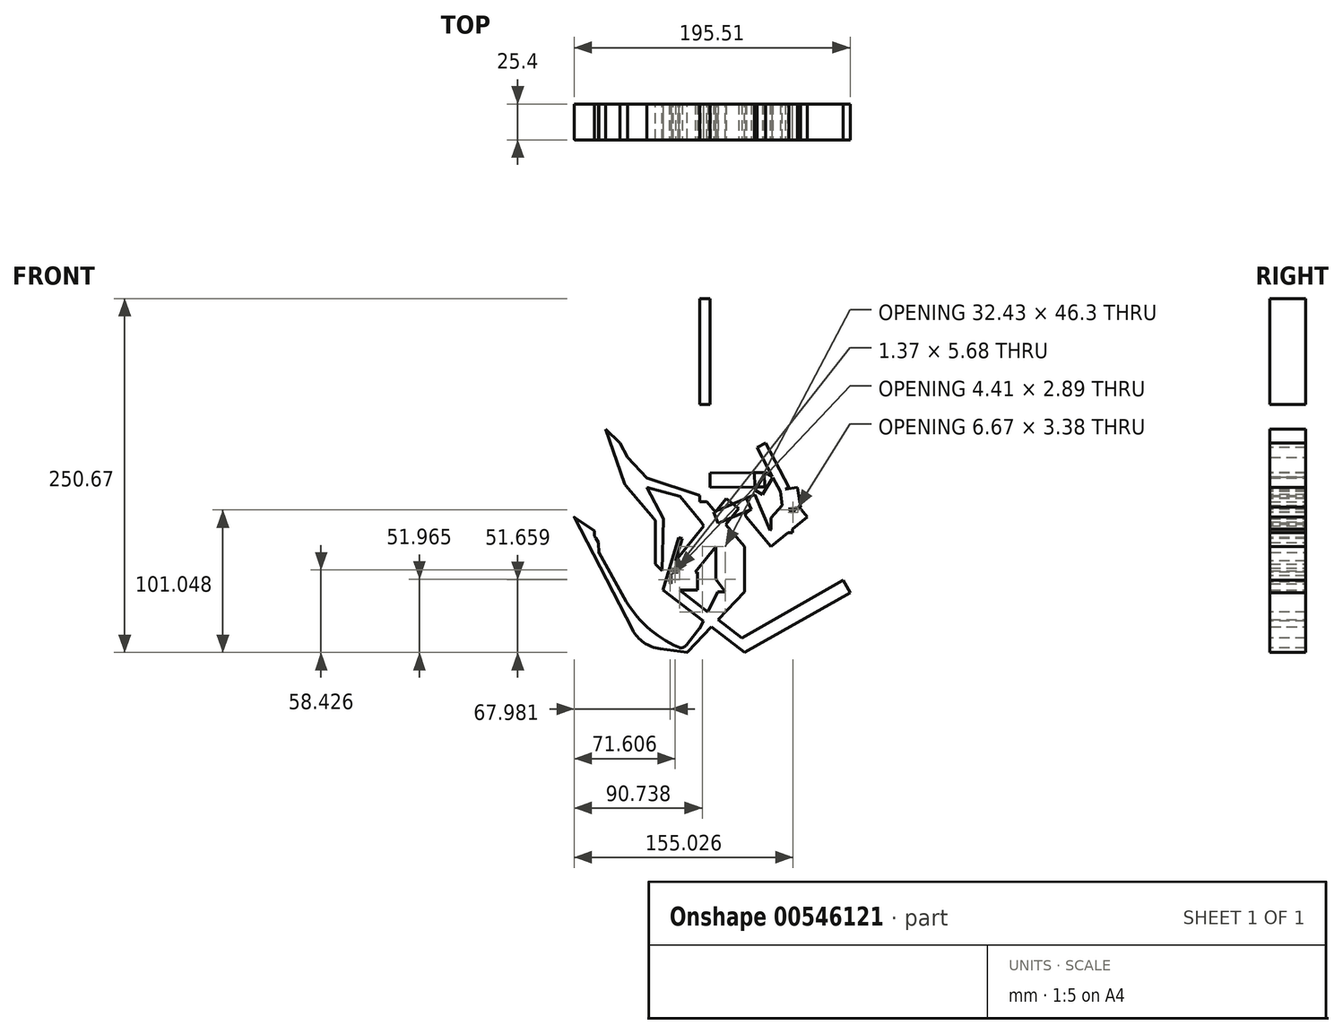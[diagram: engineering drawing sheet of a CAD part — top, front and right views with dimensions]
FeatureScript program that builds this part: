
annotation { "Feature Type Name" : "Feature", "Feature Type Description" : "" }
export const myFeature = defineFeature(function(context is Context, id is Id, definition is map)
    precondition{}
    {
        {
            var Q0;
            Q0=qCreatedBy(makeId("Front.planeOp"),FACE);
            var sketch = newSketch(context, id + "F0", { "sketchPlane" : qUnion([Q0])});
            skLineSegment(sketch, "E0", {"start": v(-82.74, 63.4) * mm, "end": v(-69.2, 48.58) * mm});
            skLineSegment(sketch, "E1", {"start": v(-69.2, 48.58) * mm, "end": v(-30.01, 35.76) * mm});
            skLineSegment(sketch, "E2", {"start": v(-30.01, 35.76) * mm, "end": v(0, 0) * mm});
            skLineSegment(sketch, "E3", {"start": v(0, 0) * mm, "end": v(0, -32.01) * mm});
            skLineSegment(sketch, "E4", {"start": v(0, -32.01) * mm, "end": v(-40.44, -74.7) * mm});
            skLineSegment(sketch, "E5", {"start": v(-40.44, -74.7) * mm, "end": v(-73.16, -70.67) * mm});
            skLineSegment(sketch, "E6", {"start": v(-73.16, -70.67) * mm, "end": v(-120.63, 20.91) * mm});
            skLineSegment(sketch, "E7", {"start": v(-120.63, 20.91) * mm, "end": v(-106.32, 11.13) * mm});
            skLineSegment(sketch, "E8", {"start": v(-106.32, 11.13) * mm, "end": v(-106.32, 7.38) * mm});
            skLineSegment(sketch, "E9", {"start": v(-106.32, 7.38) * mm, "end": v(-103.32, 2.97) * mm});
            skLineSegment(sketch, "E10", {"start": v(-103.32, 2.97) * mm, "end": v(-103.19, -3.97) * mm});
            skLineSegment(sketch, "E11", {"start": v(-103.19, -3.97) * mm, "end": v(-69.32, -65.1) * mm});
            skLineSegment(sketch, "E12", {"start": v(-69.32, -65.1) * mm, "end": v(-43.28, -72.68) * mm});
            skPoint(sketch, "E12.endSnap0", {"position": v(-56.8, -72.68) * mm});
            skLineSegment(sketch, "E13", {"start": v(-43.28, -72.68) * mm, "end": v(-31.05, -56.63) * mm});
            skLineSegment(sketch, "E14", {"start": v(-31.05, -56.63) * mm, "end": v(-19.08, -32.01) * mm});
            skLineSegment(sketch, "E15", {"start": v(-19.08, -32.01) * mm, "end": v(-19.08, -32.01) * mm});
            skLineSegment(sketch, "E16", {"start": v(-19.08, -32.01) * mm, "end": v(-13.68, -32.01) * mm});
            skLineSegment(sketch, "E17", {"start": v(-13.68, -32.01) * mm, "end": v(-20.13, -23.16) * mm});
            skLineSegment(sketch, "E18", {"start": v(-20.13, -23.16) * mm, "end": v(-20.13, 0) * mm});
            skLineSegment(sketch, "E19", {"start": v(-20.13, 0) * mm, "end": v(-30.68, 17.6) * mm});
            skLineSegment(sketch, "E20", {"start": v(-30.68, 17.6) * mm, "end": v(-45.8, 35.76) * mm});
            skLineSegment(sketch, "E21", {"start": v(-45.8, 35.76) * mm, "end": v(-69.2, 42.17) * mm});
            skPoint(sketch, "E21.endSnap0", {"position": v(-49.6, 42.17) * mm});
            skLineSegment(sketch, "E22", {"start": v(-69.2, 42.17) * mm, "end": v(-57.5, 19.66) * mm});
            skPoint(sketch, "E22.endSnap0", {"position": v(-57.5, 38.97) * mm});
            skLineSegment(sketch, "E23", {"start": v(-57.5, 19.66) * mm, "end": v(-58.4, -17.13) * mm});
            skLineSegment(sketch, "E24", {"start": v(-58.4, -17.13) * mm, "end": v(-63.03, -12.3) * mm});
            skLineSegment(sketch, "E25", {"start": v(-63.03, -12.3) * mm, "end": v(-63.03, 18.72) * mm});
            skLineSegment(sketch, "E26", {"start": v(-63.03, 18.72) * mm, "end": v(-84.74, 44.07) * mm});
            skLineSegment(sketch, "E27", {"start": v(-84.74, 44.07) * mm, "end": v(-98.24, 83.4) * mm});
            skLineSegment(sketch, "E28", {"start": v(-98.24, 83.4) * mm, "end": v(-88.14, 73.6) * mm});
            skLineSegment(sketch, "E29", {"start": v(-88.14, 73.6) * mm, "end": v(-82.74, 63.4) * mm});
            skSolve(sketch);
        }
        {
            var Q0;
            Q0 = qSketchRegion(id + "F0", true);
            extrude(context, id + "F1", {"entities" : qUnion([Q0]), "depth" : 25.4 * mm, "offsetDistance" : 25.4 * mm});
        }
        {
            var Q0;
            Q0=qCreatedBy(makeId("Front.planeOp"),FACE);
            var sketch = newSketch(context, id + "F2", { "sketchPlane" : qUnion([Q0])});
            skLineSegment(sketch, "E30", {"start": v(-23.37, 1.25) * mm, "end": v(-31.6, 175.7) * mm});
            skLineSegment(sketch, "E31", {"start": v(-31.6, 31.81) * mm, "end": v(-31.6, 175.7) * mm});
            skLineSegment(sketch, "E32", {"start": v(-31.6, 31.81) * mm, "end": v(0, 79) * mm});
            skLineSegment(sketch, "E33", {"start": v(0, 79) * mm, "end": v(-4.8, 68.48) * mm});
            skLineSegment(sketch, "E34", {"start": v(-4.8, 68.48) * mm, "end": v(-23.3, 56.48) * mm});
            skLineSegment(sketch, "E35", {"start": v(-23.3, 56.48) * mm, "end": v(-5.7, 62.48) * mm});
            skPoint(sketch, "E35.endSnap0", {"position": v(-14.05, 62.48) * mm});
            skLineSegment(sketch, "E36", {"start": v(-5.7, 62.48) * mm, "end": v(-7.77, 59.48) * mm});
            skPoint(sketch, "E36.endSnap0", {"position": v(-14.5, 59.48) * mm});
            skLineSegment(sketch, "E37", {"start": v(-7.77, 59.48) * mm, "end": v(-23.3, 52.09) * mm});
            skLineSegment(sketch, "E38", {"start": v(-23.3, 52.09) * mm, "end": v(6.19, 48.6) * mm});
            skLineSegment(sketch, "E39", {"start": v(6.19, 48.6) * mm, "end": v(10.66, 43.84) * mm});
            skLineSegment(sketch, "E40", {"start": v(10.66, 43.84) * mm, "end": v(8.42, 48.6) * mm});
            skPoint(sketch, "E40.endSnap0", {"position": v(8.42, 46.22) * mm});
            skLineSegment(sketch, "E41", {"start": v(8.42, 48.6) * mm, "end": v(17.69, 51.67) * mm});
            skLineSegment(sketch, "E42", {"start": v(17.69, 51.67) * mm, "end": v(7.48, 79) * mm});
            skLineSegment(sketch, "E43", {"start": v(7.48, 79) * mm, "end": v(14.97, 73.38) * mm});
            skLineSegment(sketch, "E44", {"start": v(14.97, 73.38) * mm, "end": v(31.48, 42.1) * mm});
            skLineSegment(sketch, "E45", {"start": v(31.48, 42.1) * mm, "end": v(31.48, 33.78) * mm});
            skLineSegment(sketch, "E46", {"start": v(31.48, 33.78) * mm, "end": v(31.48, 50.56) * mm});
            skLineSegment(sketch, "E47", {"start": v(31.48, 50.56) * mm, "end": v(37.55, 42.1) * mm});
            skLineSegment(sketch, "E48", {"start": v(37.55, 42.1) * mm, "end": v(39.7, 28.06) * mm});
            skLineSegment(sketch, "E49", {"start": v(39.7, 28.06) * mm, "end": v(29.1, 21.18) * mm});
            skLineSegment(sketch, "E50", {"start": v(29.1, 21.18) * mm, "end": v(51.16, 29.07) * mm});
            skLineSegment(sketch, "E51", {"start": v(51.16, 29.07) * mm, "end": v(58, 20.45) * mm});
            skLineSegment(sketch, "E52", {"start": v(58, 20.45) * mm, "end": v(29.37, -69.93) * mm});
            skLineSegment(sketch, "E53", {"start": v(29.37, -69.93) * mm, "end": v(31.21, -64.1) * mm});
            skLineSegment(sketch, "E54", {"start": v(31.21, -64.1) * mm, "end": v(29.37, -69.93) * mm});
            skLineSegment(sketch, "E55", {"start": v(29.37, -69.93) * mm, "end": v(29.37, -64.1) * mm});
            skLineSegment(sketch, "E56", {"start": v(-23.37, 1.25) * mm, "end": v(-31.6, 31.81) * mm});
            skLineSegment(sketch, "E57", {"start": v(-24.83, 32.17) * mm, "end": v(-19.53, 42.1) * mm});
            skLineSegment(sketch, "E58", {"start": v(-19.53, 42.1) * mm, "end": v(7.2, 42.3) * mm});
            skLineSegment(sketch, "E59", {"start": v(7.2, 42.3) * mm, "end": v(12.81, 36.85) * mm});
            skLineSegment(sketch, "E60", {"start": v(12.81, 36.85) * mm, "end": v(20.34, 49.23) * mm});
            skLineSegment(sketch, "E61", {"start": v(20.34, 49.23) * mm, "end": v(27.54, 30) * mm});
            skLineSegment(sketch, "E62", {"start": v(27.54, 30) * mm, "end": v(18.63, 20.35) * mm});
            skLineSegment(sketch, "E63", {"start": v(18.63, 20.35) * mm, "end": v(18.63, 10.06) * mm});
            skLineSegment(sketch, "E64", {"start": v(18.63, 10.06) * mm, "end": v(7.2, 36.85) * mm});
            skLineSegment(sketch, "E65", {"start": v(7.2, 36.85) * mm, "end": v(-12.23, 42.16) * mm});
            skLineSegment(sketch, "E66", {"start": v(-12.23, 42.16) * mm, "end": v(-13.02, 37.9) * mm});
            skLineSegment(sketch, "E67", {"start": v(-13.02, 37.9) * mm, "end": v(-13.03, 34.19) * mm});
            skLineSegment(sketch, "E68", {"start": v(-13.03, 34.19) * mm, "end": v(-51.99, -13.8) * mm});
            skLineSegment(sketch, "E69", {"start": v(-51.99, -13.8) * mm, "end": v(-40.75, 10) * mm});
            skLineSegment(sketch, "E70", {"start": v(-40.75, 10) * mm, "end": v(-46.61, 6.52) * mm});
            skLineSegment(sketch, "E71", {"start": v(-46.61, 6.52) * mm, "end": v(-57.6, -30.67) * mm});
            skLineSegment(sketch, "E72", {"start": v(-57.6, -30.67) * mm, "end": v(0, -74.98) * mm});
            skLineSegment(sketch, "E73", {"start": v(0, -74.98) * mm, "end": v(74.88, -32.52) * mm});
            skLineSegment(sketch, "E74", {"start": v(74.88, -32.52) * mm, "end": v(62.77, 0) * mm});
            skLineSegment(sketch, "E75", {"start": v(62.77, 0) * mm, "end": v(26.06, -11.54) * mm});
            skLineSegment(sketch, "E76", {"start": v(26.06, -11.54) * mm, "end": v(0, -51.5) * mm});
            skLineSegment(sketch, "E77", {"start": v(0, -51.5) * mm, "end": v(0, -51.5) * mm});
            skLineSegment(sketch, "E78", {"start": v(0, -51.5) * mm, "end": v(12.06, -45.08) * mm});
            skLineSegment(sketch, "E79", {"start": v(12.06, -45.08) * mm, "end": v(30.37, -10.19) * mm});
            skLineSegment(sketch, "E80", {"start": v(30.37, -10.19) * mm, "end": v(26.06, -11.54) * mm});
            skLineSegment(sketch, "E81", {"start": v(26.06, -11.54) * mm, "end": v(26.06, -11.54) * mm});
            skLineSegment(sketch, "E82", {"start": v(26.06, -11.54) * mm, "end": v(18.63, 0) * mm});
            skLineSegment(sketch, "E83", {"start": v(18.63, 0) * mm, "end": v(44.42, 21.18) * mm});
            skPoint(sketch, "E83.endSnap0", {"position": v(44.42, -5.77) * mm});
            skLineSegment(sketch, "E84", {"start": v(44.42, 21.18) * mm, "end": v(20.01, -83.7) * mm});
            skLineSegment(sketch, "E85", {"start": v(20.01, -83.7) * mm, "end": v(29.37, -69.93) * mm});
            skLineSegment(sketch, "E86", {"start": v(18.63, 0) * mm, "end": v(0, 22.68) * mm});
            skLineSegment(sketch, "E87", {"start": v(0, 22.68) * mm, "end": v(-6.46, 27.65) * mm});
            skLineSegment(sketch, "E88", {"start": v(-6.46, 27.65) * mm, "end": v(-33.23, -18) * mm});
            skLineSegment(sketch, "E89", {"start": v(-33.23, -18) * mm, "end": v(-33.23, -30.67) * mm});
            skLineSegment(sketch, "E90", {"start": v(-33.23, -30.67) * mm, "end": v(-44.34, -30.67) * mm});
            skLineSegment(sketch, "E91", {"start": v(-44.34, -30.67) * mm, "end": v(0, -69.49) * mm});
            skLineSegment(sketch, "E92", {"start": v(0, -69.49) * mm, "end": v(36.36, -50.72) * mm});
            skLineSegment(sketch, "E93", {"start": v(36.36, -50.72) * mm, "end": v(-0.83, -74.19) * mm});
            skLineSegment(sketch, "E94", {"start": v(-0.83, -74.19) * mm, "end": v(-1.85, -60.98) * mm});
            skLineSegment(sketch, "E95", {"start": v(26.06, -11.54) * mm, "end": v(58, -10.19) * mm});
            skLineSegment(sketch, "E96", {"start": v(58, -10.19) * mm, "end": v(36.36, -50.72) * mm});
            skSolve(sketch);
        }
        {
            var Q0;
            {var subQ23=sQuery(id+"F2.wireOp",EDGE,"E39");Q0=makeQuery(id+"F2.imprint","IMPRINT",FACE,{"disambiguationData":[TD([[makeQuery(id+"F2.imprint","IMPRINT",EDGE,{"derivedFrom":subQ23}),-1.0]])]});}
            var Q1;
            Q1=sQuery(id+"F2.wireOp",EDGE,"E58");
            var Q2;
            Q2=sQuery(id+"F2.wireOp",EDGE,"E74");
            var Q3;
            Q3=sQuery(id+"F2.wireOp",EDGE,"E83");
            var Q4;
            Q4=sQuery(id+"F2.wireOp",EDGE,"E50");
            var Q5;
            Q5=sQuery(id+"F2.wireOp",EDGE,"E51");
            var Q6;
            Q6=sQuery(id+"F2.wireOp",EDGE,"E91");
            var Q7;
            Q7=sQuery(id+"F2.wireOp",EDGE,"E72");
            var Q8;
            Q8=sQuery(id+"F2.wireOp",EDGE,"E68");
            var Q9;
            Q9=sQuery(id+"F2.wireOp",EDGE,"E87");
            var Q10;
            Q10=sQuery(id+"F2.wireOp",EDGE,"E64");
            var Q11;
            Q11=sQuery(id+"F2.wireOp",EDGE,"E62");
            var Q12;
            Q12=sQuery(id+"F2.wireOp",EDGE,"E63");
            var Q13;
            Q13=sQuery(id+"F2.wireOp",EDGE,"E61");
            var Q14;
            Q14=sQuery(id+"F2.wireOp",EDGE,"E59");
            var Q15;
            Q15=sQuery(id+"F2.wireOp",EDGE,"E90");
            var Q16;
            Q16=sQuery(id+"F2.wireOp",EDGE,"E89");
            var Q17;
            Q17=sQuery(id+"F2.wireOp",EDGE,"E71");
            var Q18;
            Q18=sQuery(id+"F2.wireOp",EDGE,"E69");
            var Q19;
            Q19=sQuery(id+"F2.wireOp",EDGE,"E70");
            var Q20;
            Q20=sQuery(id+"F2.wireOp",EDGE,"E31");
            var Q21;
            Q21=sQuery(id+"F2.wireOp",EDGE,"E42");
            var Q22;
            Q22=sQuery(id+"F2.wireOp",EDGE,"E43");
            var Q23;
            Q23=sQuery(id+"F2.wireOp",EDGE,"E40");
            var Q24;
            Q24=sQuery(id+"F2.wireOp",EDGE,"E60");
            var Q25;
            Q25=sQuery(id+"F2.wireOp",EDGE,"E41");
            var Q26;
            Q26=sQuery(id+"F2.wireOp",EDGE,"E48");
            var Q27;
            Q27=sQuery(id+"F2.wireOp",EDGE,"E47");
            var Q28;
            Q28=sQuery(id+"F2.wireOp",EDGE,"E44");
            var Q29;
            Q29=sQuery(id+"F2.wireOp",EDGE,"E49");
            var Q30;
            Q30=sQuery(id+"F2.wireOp",EDGE,"E96");
            var Q31;
            Q31=sQuery(id+"F2.wireOp",EDGE,"E88");
            var Q32;
            Q32=sQuery(id+"F2.wireOp",EDGE,"E86");
            var Q33;
            Q33=sQuery(id+"F2.wireOp",EDGE,"E85");
            var Q34;
            Q34=sQuery(id+"F2.wireOp",EDGE,"E73");
            var Q35;
            Q35=sQuery(id+"F2.wireOp",EDGE,"E53");
            extrude(context, id + "F3", {"entities" : qUnion([Q0]), "bodyType" : ToolBodyType.SURFACE, "surfaceEntities" : qUnion([Q1, Q2, Q3, Q4, Q5, Q6, Q7, Q8, Q9, Q10, Q11, Q12, Q13, Q14, Q15, Q16, Q17, Q18, Q19, Q20, Q21, Q22, Q23, Q24, Q25, Q26, Q27, Q28, Q29, Q30, Q31, Q32, Q33, Q34, Q35]), "depth" : 25.4 * mm, "offsetDistance" : 25.4 * mm});
        }
        {
            var Q0;
            Q0=makeQuery(id+"F3.opExtrude","SWEPT_FACE",FACE,{"disambiguationData":[OSD([sQuery(id+"F2.wireOp",EDGE,"E68")])]});
            extrude(context, id + "F4", {"entities" : qUnion([Q0]), "operationType" : NewBodyOperationType.ADD, "oppositeDirection" : true, "depth" : 11.48 * mm, "offsetDistance" : 25.4 * mm});
        }
        {
            var Q0;
            Q0=makeQuery(id+"F3.opExtrude","SWEPT_FACE",FACE,{"disambiguationData":[OSD([sQuery(id+"F2.wireOp",EDGE,"E71")])]});
            extrude(context, id + "F5", {"entities" : qUnion([Q0]), "operationType" : NewBodyOperationType.ADD, "oppositeDirection" : true, "depth" : 2.52 * mm, "offsetDistance" : 25.4 * mm});
        }
        {
            var Q0;
            Q0=makeQuery(id+"F3.opExtrude","SWEPT_FACE",FACE,{"disambiguationData":[OSD([sQuery(id+"F2.wireOp",EDGE,"E72")])]});
            extrude(context, id + "F6", {"entities" : qUnion([Q0]), "operationType" : NewBodyOperationType.ADD, "oppositeDirection" : true, "depth" : 7 * mm, "offsetDistance" : 25.4 * mm});
        }
        {
            var Q0;
            Q0=makeQuery(id+"F3.opExtrude","SWEPT_FACE",FACE,{"disambiguationData":[OSD([sQuery(id+"F2.wireOp",EDGE,"E89")])]});
            extrude(context, id + "F7", {"entities" : qUnion([Q0]), "operationType" : NewBodyOperationType.ADD, "depth" : 18.73 * mm, "offsetDistance" : 25.4 * mm});
        }
        {
            var Q0;
            {var subQ0=sQuery(id+"F0.wireOp",EDGE,"E19");var subQ29=sQuery(id+"F2.wireOp",EDGE,"E68");Q0=makeQuery(id+"F4.boolean.opBoolean","SPLIT",FACE,{"disambiguationData":[TD([makeQuery(id+"F1.opExtrude","SWEPT_FACE",FACE,{"disambiguationData":[OSD([subQ0])]})])],"derivedFrom":makeQuery(id+"F4.opExtrude","CAP_FACE",FACE,{"disambiguationData":[OSD([subQ29])],"isStart":false})});}
            extrude(context, id + "F8", {"entities" : qUnion([Q0]), "operationType" : NewBodyOperationType.ADD, "depth" : 4.4 * mm, "offsetDistance" : 25.4 * mm});
        }
        {
            var Q0;
            Q0=makeQuery(id+"F1.opExtrude","SWEPT_EDGE",EDGE,{"disambiguationData":[OSD([sQuery(id+"F0.wireOp",EDGE,"E26"),sQuery(id+"F0.wireOp",EDGE,"E27")])]});
            var Q1;
            Q1=makeQuery(id+"F1.opExtrude","SWEPT_EDGE",EDGE,{"disambiguationData":[OSD([sQuery(id+"F0.wireOp",EDGE,"E25"),sQuery(id+"F0.wireOp",EDGE,"E26")])]});
            fillet(context, id + "F9", {"entities" : qUnion([Q0, Q1]), "radius" : 5.08 * mm, "tangentPropagation" : true, "allowEdgeOverflow" : false});
        }
        {
            var Q0;
            Q0=makeQuery(id+"F1.opExtrude","SWEPT_EDGE",EDGE,{"disambiguationData":[OSD([sQuery(id+"F0.wireOp",EDGE,"E5"),sQuery(id+"F0.wireOp",EDGE,"E6")])]});
            fillet(context, id + "F10", {"entities" : qUnion([Q0]), "radius" : 25.58 * mm, "tangentPropagation" : true, "allowEdgeOverflow" : false});
        }
        {
            var Q0;
            Q0=makeQuery(id+"F1.opExtrude","SWEPT_EDGE",EDGE,{"disambiguationData":[OSD([sQuery(id+"F0.wireOp",EDGE,"E11"),sQuery(id+"F0.wireOp",EDGE,"E12")])]});
            fillet(context, id + "F11", {"entities" : qUnion([Q0]), "radius" : 81.82 * mm, "tangentPropagation" : true, "allowEdgeOverflow" : false});
        }
        {
            var Q0;
            Q0=makeQuery(id+"F11.opFillet","BLEND_EDGE",EDGE,{"blendedFrom":[makeQuery(id+"F1.opExtrude","SWEPT_EDGE",EDGE,{"disambiguationData":[OSD([sQuery(id+"F0.wireOp",EDGE,"E11"),sQuery(id+"F0.wireOp",EDGE,"E12")])]}),makeQuery(id+"F1.opExtrude","SWEPT_FACE",FACE,{"disambiguationData":[OSD([sQuery(id+"F0.wireOp",EDGE,"E13")])]})],"blendedInto":[makeQuery(id+"F1.opExtrude","SWEPT_FACE",FACE,{"disambiguationData":[OSD([sQuery(id+"F0.wireOp",EDGE,"E13")])]})]});
            fillet(context, id + "F12", {"entities" : qUnion([Q0]), "radius" : 5.08 * mm, "tangentPropagation" : true, "allowEdgeOverflow" : false});
        }
        {
            var Q0;
            Q0=makeQuery(id+"F1.opExtrude","SWEPT_EDGE",EDGE,{"disambiguationData":[OSD([sQuery(id+"F0.wireOp",EDGE,"E8"),sQuery(id+"F0.wireOp",EDGE,"E9")])]});
            fillet(context, id + "F13", {"entities" : qUnion([Q0]), "radius" : 5.08 * mm, "tangentPropagation" : true, "allowEdgeOverflow" : false});
        }
        {
            var Q0;
            Q0=makeQuery(id+"F3.opExtrude","SWEPT_EDGE",EDGE,{"disambiguationData":[OSD([sQuery(id+"F2.wireOp",VERTEX,"E71.end")])]});
            fillet(context, id + "F14", {"entities" : qUnion([Q0]), "radius" : 8.5 * mm, "tangentPropagation" : true, "allowEdgeOverflow" : false});
        }
        {
            var Q0;
            Q0=makeQuery(id+"F3.opExtrude","SWEPT_FACE",FACE,{"disambiguationData":[OSD([sQuery(id+"F2.wireOp",EDGE,"E86")])]});
            extrude(context, id + "F15", {"entities" : qUnion([Q0]), "depth" : 6.5 * mm, "offsetDistance" : 25.4 * mm});
        }
        {
            var Q0;
            Q0=makeQuery(id+"F3.opExtrude","SWEPT_FACE",FACE,{"disambiguationData":[OSD([sQuery(id+"F2.wireOp",EDGE,"E64")])]});
            extrude(context, id + "F16", {"entities" : qUnion([Q0]), "operationType" : NewBodyOperationType.ADD, "oppositeDirection" : true, "depth" : 6.33 * mm, "offsetDistance" : 25.4 * mm});
        }
        {
            var Q0;
            Q0=makeQuery(id+"F16.opExtrude","CAP_FACE",FACE,{"disambiguationData":[OSD([sQuery(id+"F2.wireOp",EDGE,"E64")])],"isStart":false});
            extrude(context, id + "F17", {"entities" : qUnion([Q0]), "depth" : 25.4 * mm, "offsetDistance" : 25.4 * mm});
        }
        {
            var Q0;
            Q0=makeQuery(id+"F3.opExtrude","SWEPT_FACE",FACE,{"disambiguationData":[OSD([sQuery(id+"F2.wireOp",EDGE,"E83")])]});
            extrude(context, id + "F18", {"entities" : qUnion([Q0]), "operationType" : NewBodyOperationType.ADD, "depth" : 9.32 * mm, "offsetDistance" : 25.4 * mm});
        }
        {
            var Q0;
            Q0=makeQuery(id+"F3.opExtrude","SWEPT_FACE",FACE,{"disambiguationData":[OSD([sQuery(id+"F2.wireOp",EDGE,"E63")])]});
            extrude(context, id + "F19", {"entities" : qUnion([Q0]), "operationType" : NewBodyOperationType.ADD, "oppositeDirection" : true, "depth" : 15.36 * mm, "offsetDistance" : 25.4 * mm});
        }
        {
            var Q0;
            Q0=makeQuery(id+"F3.opExtrude","SWEPT_FACE",FACE,{"disambiguationData":[OSD([sQuery(id+"F2.wireOp",EDGE,"E48")])]});
            extrude(context, id + "F20", {"entities" : qUnion([Q0]), "operationType" : NewBodyOperationType.ADD, "depth" : 12.55 * mm, "offsetDistance" : 25.4 * mm});
        }
        {
            var Q0;
            Q0=makeQuery(id+"F3.opExtrude","SWEPT_FACE",FACE,{"disambiguationData":[OSD([sQuery(id+"F2.wireOp",EDGE,"E62")])]});
            extrude(context, id + "F21", {"entities" : qUnion([Q0]), "operationType" : NewBodyOperationType.ADD, "oppositeDirection" : true, "depth" : 14.77 * mm, "offsetDistance" : 25.4 * mm});
        }
        {
            var Q0;
            Q0=makeQuery(id+"F3.opExtrude","SWEPT_EDGE",EDGE,{"disambiguationData":[OSD([sQuery(id+"F2.wireOp",VERTEX,"E86.end")])]});
            fillet(context, id + "F22", {"entities" : qUnion([Q0]), "radius" : 2537.1 * mm, "tangentPropagation" : true, "allowEdgeOverflow" : false});
        }
        {
            var Q0;
            Q0=makeQuery(id+"F15.opExtrude","CAP_EDGE",EDGE,{"disambiguationData":[OSD([sQuery(id+"F2.wireOp",VERTEX,"E86.end")])],"isStart":true});
            fillet(context, id + "F23", {"entities" : qUnion([Q0]), "radius" : 1.79 * mm, "tangentPropagation" : true, "allowEdgeOverflow" : false});
        }
        {
            var Q0;
            Q0=makeQuery(id+"F3.opExtrude","SWEPT_FACE",FACE,{"disambiguationData":[OSD([sQuery(id+"F2.wireOp",EDGE,"E44")])]});
            extrude(context, id + "F24", {"entities" : qUnion([Q0]), "operationType" : NewBodyOperationType.ADD, "depth" : 6.88 * mm, "offsetDistance" : 25.4 * mm});
        }
        {
            var Q0;
            Q0=makeQuery(id+"F3.opExtrude","SWEPT_FACE",FACE,{"disambiguationData":[OSD([sQuery(id+"F2.wireOp",EDGE,"E60")])]});
            extrude(context, id + "F25", {"entities" : qUnion([Q0]), "operationType" : NewBodyOperationType.ADD, "oppositeDirection" : true, "depth" : 6.4 * mm, "offsetDistance" : 25.4 * mm});
        }
        {
            var Q0;
            Q0=makeQuery(id+"F3.opExtrude","SWEPT_FACE",FACE,{"disambiguationData":[OSD([sQuery(id+"F2.wireOp",EDGE,"E58")])]});
            extrude(context, id + "F26", {"entities" : qUnion([Q0]), "oppositeDirection" : true, "depth" : 10.21 * mm, "offsetDistance" : 25.4 * mm});
        }
        {
            var Q0;
            Q0=makeQuery(id+"F26.opExtrude","SWEPT_FACE",FACE,{"disambiguationData":[OSD([sQuery(id+"F2.wireOp",VERTEX,"E59.start")])]});
            extrude(context, id + "F27", {"entities" : qUnion([Q0]), "depth" : 7.04 * mm, "offsetDistance" : 25.4 * mm});
        }
        {
            var Q0;
            Q0=makeQuery(id+"F3.opExtrude","SWEPT_FACE",FACE,{"disambiguationData":[OSD([sQuery(id+"F2.wireOp",EDGE,"E73")])]});
            extrude(context, id + "F28", {"entities" : qUnion([Q0]), "operationType" : NewBodyOperationType.ADD, "oppositeDirection" : true, "depth" : 9.97 * mm, "offsetDistance" : 25.4 * mm});
        }
        {
            var Q0;
            Q0=makeQuery(id+"F22.opFillet","BLEND_EDGE",EDGE,{"blendedFrom":[makeQuery(id+"F3.opExtrude","SWEPT_EDGE",EDGE,{"disambiguationData":[OSD([sQuery(id+"F2.wireOp",VERTEX,"E86.end")])]}),makeQuery(id+"F3.opExtrude","SWEPT_FACE",FACE,{"disambiguationData":[OSD([sQuery(id+"F2.wireOp",EDGE,"E83")])]})],"blendedInto":[makeQuery(id+"F3.opExtrude","SWEPT_FACE",FACE,{"disambiguationData":[OSD([sQuery(id+"F2.wireOp",EDGE,"E83")])]})]});
            fillet(context, id + "F29", {"entities" : qUnion([Q0]), "radius" : 18.16 * mm, "tangentPropagation" : true, "allowEdgeOverflow" : false});
        }
        {
            var Q0;
            Q0=makeQuery(id+"F26.opExtrude","SWEPT_FACE",FACE,{"disambiguationData":[OSD([sQuery(id+"F2.wireOp",VERTEX,"E58.start")])]});
            extrude(context, id + "F30", {"entities" : qUnion([Q0]), "operationType" : NewBodyOperationType.ADD, "depth" : 10.53 * mm, "offsetDistance" : 25.4 * mm});
        }
        {
            var Q0;
            Q0=makeQuery(id+"F3.opExtrude","SWEPT_FACE",FACE,{"disambiguationData":[OSD([sQuery(id+"F2.wireOp",EDGE,"E31")])]});
            extrude(context, id + "F31", {"entities" : qUnion([Q0]), "depth" : 7.2 * mm, "offsetDistance" : 25.4 * mm});
        }
        {
            var Q0;
            Q0=makeQuery(id+"F3.opExtrude","SWEPT_EDGE",EDGE,{"disambiguationData":[OSD([sQuery(id+"F2.wireOp",VERTEX,"E44.start")])]});
            fillet(context, id + "F32", {"entities" : qUnion([Q0]), "radius" : 25.4 * mm, "tangentPropagation" : true, "allowEdgeOverflow" : false});
        }
        {
            var Q0;
            Q0=makeQuery(id+"F31.opExtrude","SWEPT_FACE",FACE,{"disambiguationData":[OSD([sQuery(id+"F2.wireOp",VERTEX,"E31.start")])]});
            extrude(context, id + "F33", {"entities" : qUnion([Q0]), "operationType" : NewBodyOperationType.REMOVE, "oppositeDirection" : true, "depth" : 68.83 * mm, "offsetDistance" : 25.4 * mm});
        }
        {
            var Q0;
            Q0=makeQuery(id+"F3.opExtrude","SWEPT_BODY",BODY,{"disambiguationData":[OSD([sQuery(id+"F2.wireOp",EDGE,"E31")])]});
            deleteBodies(context, id + "F34", {"entities" : qUnion([Q0])});
        }
        {
            var Q0;
            Q0=makeQuery(id+"F1.opExtrude","CAP_EDGE",EDGE,{"disambiguationData":[OSD([sQuery(id+"F0.wireOp",EDGE,"E6")])],"isStart":false});
            var Q1;
            {var subQ0=sQuery(id+"F0.wireOp",EDGE,"E19");var subQ1=sQuery(id+"F2.wireOp",EDGE,"E68");var subQ2=makeQuery(id+"F3.opExtrude","CAP_EDGE",EDGE,{"disambiguationData":[OSD([subQ1])],"isStart":false});var subQ3=makeQuery(id+"F4.opExtrude","SWEPT_FACE",FACE,{"disambiguationData":[OSD([subQ1]),TDD([subQ2])]});var subQ4=sQuery(id+"F0.wireOp",EDGE,"E6");var subQ5=sQuery(id+"F0.wireOp",EDGE,"E5");var subQ6=makeQuery(id+"F1.opExtrude","CAP_FACE",FACE,{"disambiguationData":[OSD([sQuery(id+"F0.wireOp",EDGE,"E0"),sQuery(id+"F0.wireOp",EDGE,"E1"),sQuery(id+"F0.wireOp",EDGE,"E2"),sQuery(id+"F0.wireOp",EDGE,"E3"),sQuery(id+"F0.wireOp",EDGE,"E4"),subQ5,subQ4,sQuery(id+"F0.wireOp",EDGE,"E7"),sQuery(id+"F0.wireOp",EDGE,"E8"),sQuery(id+"F0.wireOp",EDGE,"E9"),sQuery(id+"F0.wireOp",EDGE,"E10"),sQuery(id+"F0.wireOp",EDGE,"E11"),sQuery(id+"F0.wireOp",EDGE,"E12"),sQuery(id+"F0.wireOp",EDGE,"E13"),sQuery(id+"F0.wireOp",EDGE,"E14"),sQuery(id+"F0.wireOp",EDGE,"E16"),sQuery(id+"F0.wireOp",EDGE,"E17"),sQuery(id+"F0.wireOp",EDGE,"E18"),subQ0,sQuery(id+"F0.wireOp",EDGE,"E20"),sQuery(id+"F0.wireOp",EDGE,"E21"),sQuery(id+"F0.wireOp",EDGE,"E22"),sQuery(id+"F0.wireOp",EDGE,"E23"),sQuery(id+"F0.wireOp",EDGE,"E24"),sQuery(id+"F0.wireOp",EDGE,"E25"),sQuery(id+"F0.wireOp",EDGE,"E26"),sQuery(id+"F0.wireOp",EDGE,"E27"),sQuery(id+"F0.wireOp",EDGE,"E28"),sQuery(id+"F0.wireOp",EDGE,"E29")])],"isStart":false});var subQ7=sQuery(id+"F2.wireOp",EDGE,"E89");var subQ8=sQuery(id+"F2.wireOp",EDGE,"E72");var subQ9=sQuery(id+"F2.wireOp",EDGE,"E71");Q1=makeQuery(id+"F10.opFillet","BLEND_EDGE",EDGE,{"blendedFrom":[makeQuery(id+"F1.opExtrude","SWEPT_EDGE",EDGE,{"disambiguationData":[OSD([subQ5,subQ4])]}),makeQuery(id+"F8.boolean.opBoolean","MERGE",FACE,{"derivedFrom":[makeQuery(id+"F7.boolean.opBoolean","MERGE",FACE,{"derivedFrom":[makeQuery(id+"F6.boolean.opBoolean","MERGE",FACE,{"derivedFrom":[makeQuery(id+"F5.boolean.opBoolean","MERGE",FACE,{"derivedFrom":[makeQuery(id+"F4.boolean.opBoolean","MERGE",FACE,{"derivedFrom":[subQ6,subQ3]}),makeQuery(id+"F5.opExtrude","SWEPT_FACE",FACE,{"disambiguationData":[OSD([subQ9]),TDD([makeQuery(id+"F3.opExtrude","CAP_EDGE",EDGE,{"disambiguationData":[OSD([subQ9])],"isStart":false})])]})]}),makeQuery(id+"F6.opExtrude","SWEPT_FACE",FACE,{"disambiguationData":[OSD([subQ8]),TDD([makeQuery(id+"F3.opExtrude","CAP_EDGE",EDGE,{"disambiguationData":[OSD([subQ8])],"isStart":false})])]})]}),makeQuery(id+"F7.opExtrude","SWEPT_FACE",FACE,{"disambiguationData":[OSD([subQ7]),TDD([makeQuery(id+"F3.opExtrude","CAP_EDGE",EDGE,{"disambiguationData":[OSD([subQ7])],"isStart":false})])]})]}),makeQuery(id+"F8.opExtrude","SWEPT_FACE",FACE,{"disambiguationData":[OSD([subQ1]),TDD([makeQuery(id+"F4.boolean.opBoolean","SPLIT",EDGE,{"disambiguationData":[TD([makeQuery(id+"F1.opExtrude","SWEPT_FACE",FACE,{"disambiguationData":[OSD([subQ0])]})])],"derivedFrom":makeQuery(id+"F4.opExtrude","CAP_EDGE",EDGE,{"disambiguationData":[OSD([subQ1]),TDD([subQ2])],"isStart":false})})])]})]})],"blendedInto":[makeQuery(id+"F8.boolean.opBoolean","MERGE",FACE,{"derivedFrom":[makeQuery(id+"F7.boolean.opBoolean","MERGE",FACE,{"derivedFrom":[makeQuery(id+"F6.boolean.opBoolean","MERGE",FACE,{"derivedFrom":[makeQuery(id+"F5.boolean.opBoolean","MERGE",FACE,{"derivedFrom":[makeQuery(id+"F4.boolean.opBoolean","MERGE",FACE,{"derivedFrom":[subQ6,subQ3]}),makeQuery(id+"F5.opExtrude","SWEPT_FACE",FACE,{"disambiguationData":[OSD([subQ9]),TDD([makeQuery(id+"F3.opExtrude","CAP_EDGE",EDGE,{"disambiguationData":[OSD([subQ9])],"isStart":false})])]})]}),makeQuery(id+"F6.opExtrude","SWEPT_FACE",FACE,{"disambiguationData":[OSD([subQ8]),TDD([makeQuery(id+"F3.opExtrude","CAP_EDGE",EDGE,{"disambiguationData":[OSD([subQ8])],"isStart":false})])]})]}),makeQuery(id+"F7.opExtrude","SWEPT_FACE",FACE,{"disambiguationData":[OSD([subQ7]),TDD([makeQuery(id+"F3.opExtrude","CAP_EDGE",EDGE,{"disambiguationData":[OSD([subQ7])],"isStart":false})])]})]}),makeQuery(id+"F8.opExtrude","SWEPT_FACE",FACE,{"disambiguationData":[OSD([subQ1]),TDD([makeQuery(id+"F4.boolean.opBoolean","SPLIT",EDGE,{"disambiguationData":[TD([makeQuery(id+"F1.opExtrude","SWEPT_FACE",FACE,{"disambiguationData":[OSD([subQ0])]})])],"derivedFrom":makeQuery(id+"F4.opExtrude","CAP_EDGE",EDGE,{"disambiguationData":[OSD([subQ1]),TDD([subQ2])],"isStart":false})})])]})]})]});}
            var Q2;
            {var subQ0=sQuery(id+"F0.wireOp",EDGE,"E19");var subQ1=sQuery(id+"F2.wireOp",EDGE,"E68");var subQ2=makeQuery(id+"F3.opExtrude","CAP_EDGE",EDGE,{"disambiguationData":[OSD([subQ1])],"isStart":false});var subQ3=makeQuery(id+"F4.opExtrude","SWEPT_FACE",FACE,{"disambiguationData":[OSD([subQ1]),TDD([subQ2])]});var subQ4=sQuery(id+"F0.wireOp",EDGE,"E13");var subQ5=sQuery(id+"F0.wireOp",EDGE,"E12");var subQ6=sQuery(id+"F0.wireOp",EDGE,"E11");var subQ7=makeQuery(id+"F1.opExtrude","CAP_FACE",FACE,{"disambiguationData":[OSD([sQuery(id+"F0.wireOp",EDGE,"E0"),sQuery(id+"F0.wireOp",EDGE,"E1"),sQuery(id+"F0.wireOp",EDGE,"E2"),sQuery(id+"F0.wireOp",EDGE,"E3"),sQuery(id+"F0.wireOp",EDGE,"E4"),sQuery(id+"F0.wireOp",EDGE,"E5"),sQuery(id+"F0.wireOp",EDGE,"E6"),sQuery(id+"F0.wireOp",EDGE,"E7"),sQuery(id+"F0.wireOp",EDGE,"E8"),sQuery(id+"F0.wireOp",EDGE,"E9"),sQuery(id+"F0.wireOp",EDGE,"E10"),subQ6,subQ5,subQ4,sQuery(id+"F0.wireOp",EDGE,"E14"),sQuery(id+"F0.wireOp",EDGE,"E16"),sQuery(id+"F0.wireOp",EDGE,"E17"),sQuery(id+"F0.wireOp",EDGE,"E18"),subQ0,sQuery(id+"F0.wireOp",EDGE,"E20"),sQuery(id+"F0.wireOp",EDGE,"E21"),sQuery(id+"F0.wireOp",EDGE,"E22"),sQuery(id+"F0.wireOp",EDGE,"E23"),sQuery(id+"F0.wireOp",EDGE,"E24"),sQuery(id+"F0.wireOp",EDGE,"E25"),sQuery(id+"F0.wireOp",EDGE,"E26"),sQuery(id+"F0.wireOp",EDGE,"E27"),sQuery(id+"F0.wireOp",EDGE,"E28"),sQuery(id+"F0.wireOp",EDGE,"E29")])],"isStart":false});var subQ8=sQuery(id+"F2.wireOp",EDGE,"E89");var subQ9=sQuery(id+"F2.wireOp",EDGE,"E72");var subQ10=sQuery(id+"F2.wireOp",EDGE,"E71");Q2=makeQuery(id+"F12.opFillet","BLEND_EDGE",EDGE,{"blendedFrom":[makeQuery(id+"F11.opFillet","BLEND_EDGE",EDGE,{"blendedFrom":[makeQuery(id+"F1.opExtrude","SWEPT_EDGE",EDGE,{"disambiguationData":[OSD([subQ6,subQ5])]}),makeQuery(id+"F1.opExtrude","SWEPT_FACE",FACE,{"disambiguationData":[OSD([subQ4])]})],"blendedInto":[makeQuery(id+"F1.opExtrude","SWEPT_FACE",FACE,{"disambiguationData":[OSD([subQ4])]})]}),makeQuery(id+"F8.boolean.opBoolean","MERGE",FACE,{"derivedFrom":[makeQuery(id+"F7.boolean.opBoolean","MERGE",FACE,{"derivedFrom":[makeQuery(id+"F6.boolean.opBoolean","MERGE",FACE,{"derivedFrom":[makeQuery(id+"F5.boolean.opBoolean","MERGE",FACE,{"derivedFrom":[makeQuery(id+"F4.boolean.opBoolean","MERGE",FACE,{"derivedFrom":[subQ7,subQ3]}),makeQuery(id+"F5.opExtrude","SWEPT_FACE",FACE,{"disambiguationData":[OSD([subQ10]),TDD([makeQuery(id+"F3.opExtrude","CAP_EDGE",EDGE,{"disambiguationData":[OSD([subQ10])],"isStart":false})])]})]}),makeQuery(id+"F6.opExtrude","SWEPT_FACE",FACE,{"disambiguationData":[OSD([subQ9]),TDD([makeQuery(id+"F3.opExtrude","CAP_EDGE",EDGE,{"disambiguationData":[OSD([subQ9])],"isStart":false})])]})]}),makeQuery(id+"F7.opExtrude","SWEPT_FACE",FACE,{"disambiguationData":[OSD([subQ8]),TDD([makeQuery(id+"F3.opExtrude","CAP_EDGE",EDGE,{"disambiguationData":[OSD([subQ8])],"isStart":false})])]})]}),makeQuery(id+"F8.opExtrude","SWEPT_FACE",FACE,{"disambiguationData":[OSD([subQ1]),TDD([makeQuery(id+"F4.boolean.opBoolean","SPLIT",EDGE,{"disambiguationData":[TD([makeQuery(id+"F1.opExtrude","SWEPT_FACE",FACE,{"disambiguationData":[OSD([subQ0])]})])],"derivedFrom":makeQuery(id+"F4.opExtrude","CAP_EDGE",EDGE,{"disambiguationData":[OSD([subQ1]),TDD([subQ2])],"isStart":false})})])]})]})],"blendedInto":[makeQuery(id+"F8.boolean.opBoolean","MERGE",FACE,{"derivedFrom":[makeQuery(id+"F7.boolean.opBoolean","MERGE",FACE,{"derivedFrom":[makeQuery(id+"F6.boolean.opBoolean","MERGE",FACE,{"derivedFrom":[makeQuery(id+"F5.boolean.opBoolean","MERGE",FACE,{"derivedFrom":[makeQuery(id+"F4.boolean.opBoolean","MERGE",FACE,{"derivedFrom":[subQ7,subQ3]}),makeQuery(id+"F5.opExtrude","SWEPT_FACE",FACE,{"disambiguationData":[OSD([subQ10]),TDD([makeQuery(id+"F3.opExtrude","CAP_EDGE",EDGE,{"disambiguationData":[OSD([subQ10])],"isStart":false})])]})]}),makeQuery(id+"F6.opExtrude","SWEPT_FACE",FACE,{"disambiguationData":[OSD([subQ9]),TDD([makeQuery(id+"F3.opExtrude","CAP_EDGE",EDGE,{"disambiguationData":[OSD([subQ9])],"isStart":false})])]})]}),makeQuery(id+"F7.opExtrude","SWEPT_FACE",FACE,{"disambiguationData":[OSD([subQ8]),TDD([makeQuery(id+"F3.opExtrude","CAP_EDGE",EDGE,{"disambiguationData":[OSD([subQ8])],"isStart":false})])]})]}),makeQuery(id+"F8.opExtrude","SWEPT_FACE",FACE,{"disambiguationData":[OSD([subQ1]),TDD([makeQuery(id+"F4.boolean.opBoolean","SPLIT",EDGE,{"disambiguationData":[TD([makeQuery(id+"F1.opExtrude","SWEPT_FACE",FACE,{"disambiguationData":[OSD([subQ0])]})])],"derivedFrom":makeQuery(id+"F4.opExtrude","CAP_EDGE",EDGE,{"disambiguationData":[OSD([subQ1]),TDD([subQ2])],"isStart":false})})])]})]})]});}
            fillet(context, id + "F35", {"entities" : qUnion([Q0, Q1, Q2]), "radius" : 0.31 * mm, "tangentPropagation" : true, "allowEdgeOverflow" : false});
        }
    });
